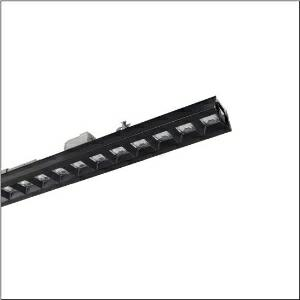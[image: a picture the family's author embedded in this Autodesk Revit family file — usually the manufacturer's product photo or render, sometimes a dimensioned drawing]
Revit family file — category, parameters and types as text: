
# Revit family: licross_r__21_silica_51ts12dn4zm00582xx_af91
name_source: partatom
category: Lighting Fixtures
units: mm (PartAtom-declared; Revit-internal decimal feet)

## family parameters
Cut with Voids When Loaded = No
Host = Face
Light Source = No
Part Type = Normal
Room Calculation Point = No
Round Connector Dimension = Use Diameter
Shared = No

## types (1)
- --- (1 x LED, 6340 lm, 39 W, 4000K)
    Apparent Load = 39 VA
    CIE Flux Codes = 86 100 100 100 100
    Color Rendering = 80
    Color Temperature = 4000K
    Default Elevation = 1800 mm
    Description = Licross® 21 Silica, luminaire insert, of sheet steel, galvanised, black, length: 1.500mm, width: 82mm, height: 86mm, LED rated luminous flux: 6.340lm, light colour: 840, control gear: DALI 2, with plug, 5-pole, with phase selection, mains connection: 220..240V, AC, 50/60Hz, rated input power: 39W, halogen-free wiring, primary light control with lens, of PMMA, primary anti-glare with darklight reflector, of PC, CAT 2 (L<= 1000cd/m²), light emission: direct distribution, primary light characteristic: symmetric, protection rating (complete): IP40, insulation class (complete): insulation class I (protective earthing), certification: CE, UKCA, protection symbol: D if used in an environment without relevant dust loads, impact resistance: IK03, permissible ambient temperature for indoor applications: -25..+45°C, corresponds to IFS (International Featured Standards) requirements for safety and quality in the food industry, reducing of maximum allowable ambient temperature of 5°C with ceiling mounting, LABS conformity tested according to VDMA 24364:2018-05, packaging unit: 1 piece
    Height = 86 mm
    Lamp = 1 x LED
    Lamp Light Flux = 6340 lm
    Lamp Power = 39 W
    Lamp count = 1
    Length = 1500 mm
    Luminous efficacy = 163 lm/W
    Manufacturer = Siteco
    ModVariant = No
    Model = 51TS12DN4ZM00582XX
    Mounting Place = Ceiling
    Mounting Type = Pendant
    Number of Poles = 1
    OnlyDefault = Yes
    Power Factor = 1
    Product Name = Licross® 21 Silica
    Product group = luminaire insert
    ProductGroupID = 902
    Protection Class = Protection class I
    Protection Degree = IP 40
    RLX_Detail_Level = 1
    RLX_Emergency_Light_Flux = 0 lm
    RLX_Emergency_Type = 0
    RLX_Emergency_Type_DB = No
    RlxData = <blob elided: 55917 chars, md5=3a950621>
    Socket = socket
    Standby Power = 0 W
    System Light Flux = 6340 lm
    System Power = 39 W
    Type Comments = factory setting: luminous flux: 100 % | dim-lin: 254 | 435 mA
    Type Image = l_1290829.jpg
    URL = http://relux.com
    VarID = @adj_106436
    Voltage = 0 V
    Weight = 0.00 kg
    Width = 82 mm  [stored 0.269029 ft]

note: [stored X ft] marks values corroborated as IEEE doubles in the binary element streams (Revit-internal decimal feet)

## geometry (parser evidence)
native form markers: Blend x4, Sweep x12
no freeform markers — native parametric forms only
